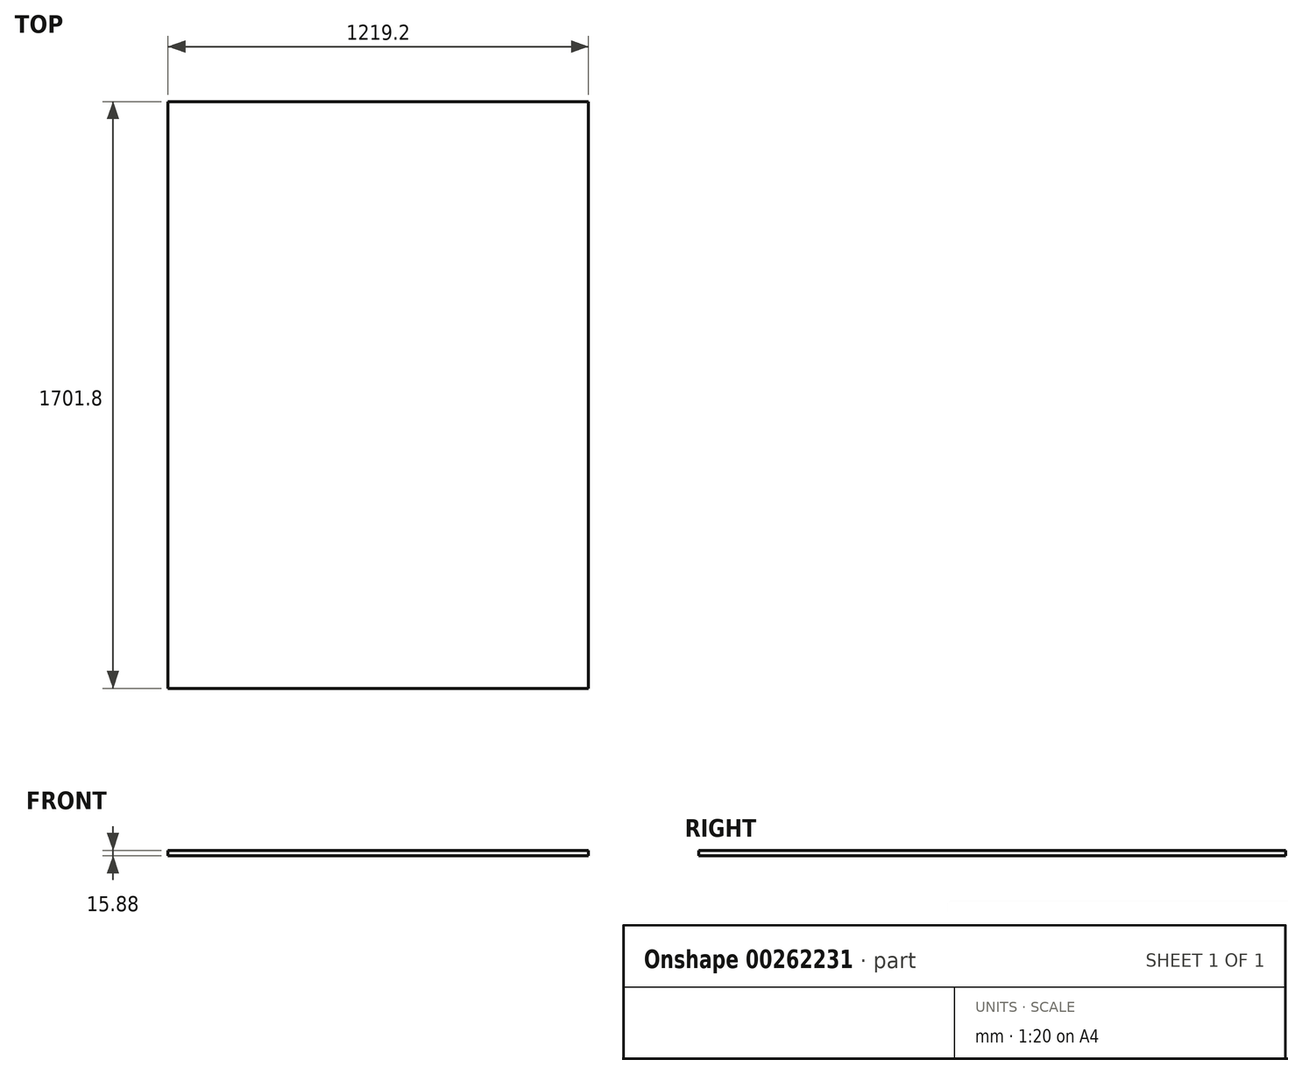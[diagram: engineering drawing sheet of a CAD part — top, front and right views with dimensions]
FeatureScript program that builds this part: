
annotation { "Feature Type Name" : "Feature", "Feature Type Description" : "" }
export const myFeature = defineFeature(function(context is Context, id is Id, definition is map)
    precondition{}
    {
        {
            var Q0;
            Q0=qCreatedBy(makeId("Top.planeOp"),FACE);
            var sketch = newSketch(context, id + "F0", { "sketchPlane" : qUnion([Q0])});
            skLineSegment(sketch, "E0.bottom", {"start": v(609.6, -850.9) * mm, "end": v(-609.6, -850.9) * mm});
            skLineSegment(sketch, "E0.top", {"start": v(609.6, 850.9) * mm, "end": v(-609.6, 850.9) * mm});
            skLineSegment(sketch, "E0.left", {"start": v(609.6, -850.9) * mm, "end": v(609.6, 850.9) * mm});
            skLineSegment(sketch, "E0.right", {"start": v(-609.6, -850.9) * mm, "end": v(-609.6, 850.9) * mm});
            skPoint(sketch, "E0.middle", {"position": v(0, 0) * mm});
            skSolve(sketch);
        }
        {
            var Q0;
            Q0=makeQuery(id+"F0.imprint","IMPRINT",FACE,{"disambiguationData":[TD([[makeQuery(id+"F0.imprint","IMPRINT",EDGE,{"derivedFrom":sQuery(id+"F0.wireOp",EDGE,"E0.bottom")}),-1.0]])]});
            extrude(context, id + "F1", {"entities" : qUnion([Q0]), "depth" : 15.88 * mm});
        }
    });
